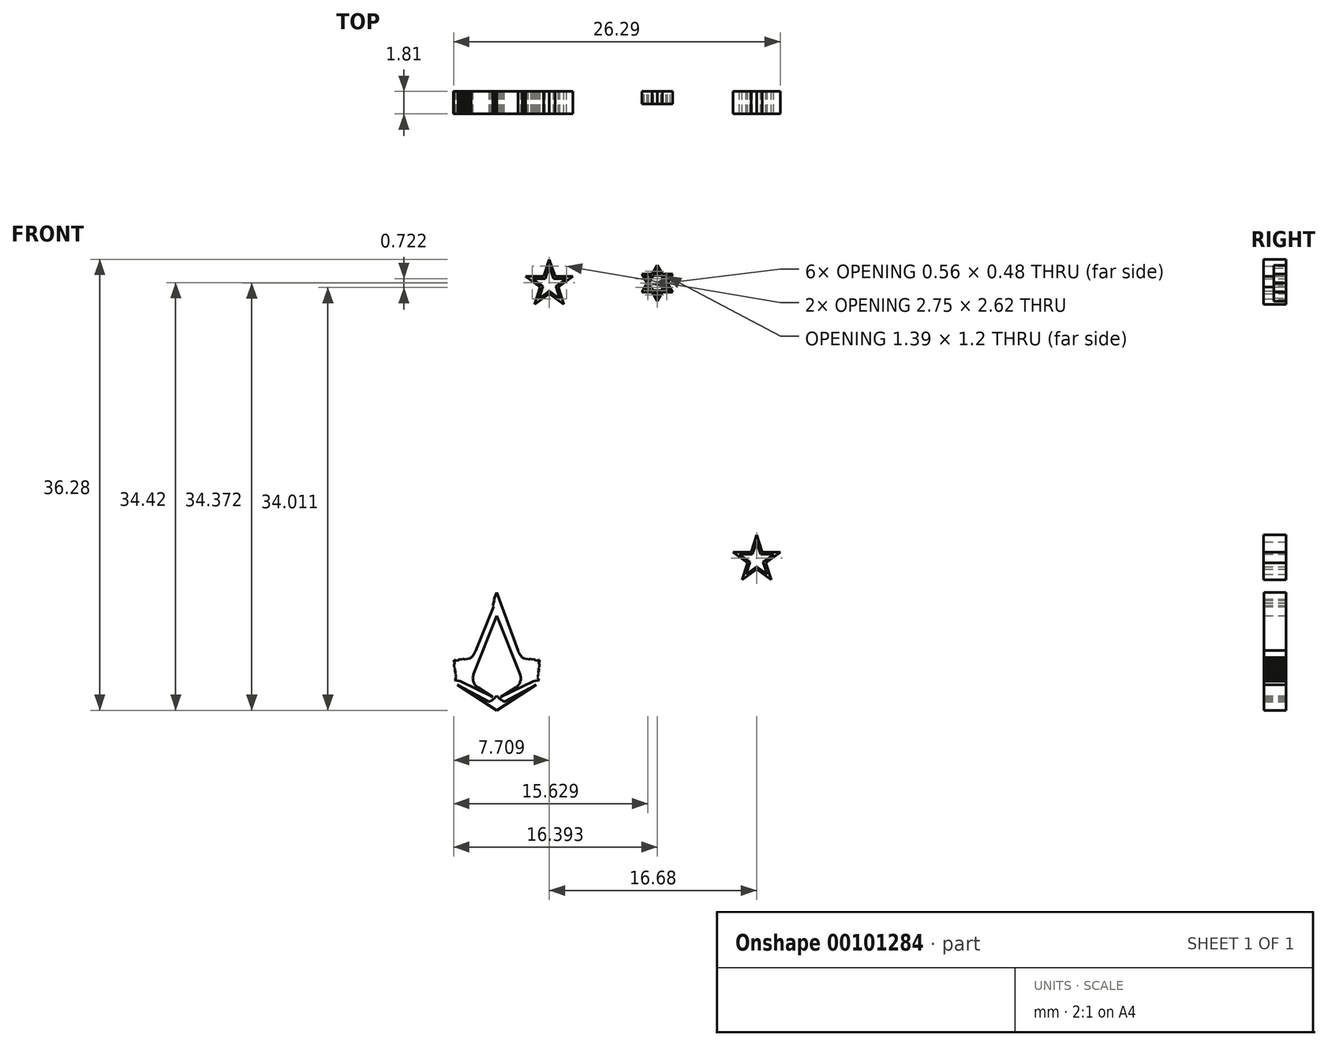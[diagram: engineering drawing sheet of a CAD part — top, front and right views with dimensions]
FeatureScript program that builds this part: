
annotation { "Feature Type Name" : "Feature", "Feature Type Description" : "" }
export const myFeature = defineFeature(function(context is Context, id is Id, definition is map)
    precondition{}
    {
        {
            var Q0;
            Q0=qCreatedBy(makeId("Front.planeOp"),FACE);
            var sketch = newSketch(context, id + "F0", { "sketchPlane" : qUnion([Q0])});
            skLineSegment(sketch, "E0", {"start": v(-3.78, 9.8) * mm, "end": v(-3.78, -0.73) * mm});
            skLineSegment(sketch, "E1", {"start": v(-3.78, 9.8) * mm, "end": v(-3.78, 11.8) * mm});
            skLineSegment(sketch, "E2", {"start": v(-3.78, 9.8) * mm, "end": v(-4, 9.25) * mm});
            skLineSegment(sketch, "E3", {"start": v(-4, 9.25) * mm, "end": v(-3.96, 9.16) * mm});
            skLineSegment(sketch, "E4", {"start": v(-3.96, 9.16) * mm, "end": v(-4.04, 8.97) * mm});
            skLineSegment(sketch, "E5", {"start": v(-4.04, 8.97) * mm, "end": v(-4.02, 8.93) * mm});
            skLineSegment(sketch, "E6", {"start": v(-4.02, 8.93) * mm, "end": v(-4.1, 8.75) * mm});
            skLineSegment(sketch, "E7", {"start": v(-4.1, 8.75) * mm, "end": v(-4.05, 8.65) * mm});
            skLineSegment(sketch, "E8", {"start": v(-4.05, 8.65) * mm, "end": v(-5.48, 5.12) * mm});
            skArc(sketch, "E9", {"start": v(-5.84, 4.56) * mm, "mid": v(-5.63, 4.83) * mm, "end": v(-5.48, 5.12) * mm});
            skArc(sketch, "E10", {"start": v(-6.03, 4.5) * mm, "mid": v(-5.92, 4.51) * mm, "end": v(-5.84, 4.56) * mm});
            skLineSegment(sketch, "E11", {"start": v(-6.03, 4.5) * mm, "end": v(-6.09, 4.43) * mm});
            skLineSegment(sketch, "E12", {"start": v(-6.09, 4.43) * mm, "end": v(-6.24, 4.47) * mm});
            skLineSegment(sketch, "E13", {"start": v(-6.24, 4.47) * mm, "end": v(-6.32, 4.39) * mm});
            skLineSegment(sketch, "E14", {"start": v(-6.32, 4.39) * mm, "end": v(-6.53, 4.46) * mm});
            skLineSegment(sketch, "E15", {"start": v(-6.53, 4.46) * mm, "end": v(-6.6, 4.4) * mm});
            skLineSegment(sketch, "E16", {"start": v(-6.6, 4.4) * mm, "end": v(-6.79, 4.45) * mm});
            skLineSegment(sketch, "E17", {"start": v(-6.79, 4.45) * mm, "end": v(-6.9, 4.3) * mm});
            skLineSegment(sketch, "E18", {"start": v(-6.9, 4.3) * mm, "end": v(-7.24, 4.37) * mm});
            skLineSegment(sketch, "E19", {"start": v(-7.24, 4.37) * mm, "end": v(-7.18, 4.16) * mm});
            skLineSegment(sketch, "E20", {"start": v(-7.18, 4.16) * mm, "end": v(-7.18, 4.03) * mm});
            skLineSegment(sketch, "E21", {"start": v(-7.18, 4.03) * mm, "end": v(-7.26, 3.94) * mm});
            skLineSegment(sketch, "E22", {"start": v(-7.26, 3.94) * mm, "end": v(-7.14, 3.79) * mm});
            skLineSegment(sketch, "E23", {"start": v(-7.14, 3.79) * mm, "end": v(-7.21, 3.7) * mm});
            skLineSegment(sketch, "E24", {"start": v(-7.21, 3.7) * mm, "end": v(-7.1, 3.54) * mm});
            skLineSegment(sketch, "E25", {"start": v(-7.1, 3.54) * mm, "end": v(-7.18, 3.4) * mm});
            skLineSegment(sketch, "E26", {"start": v(-7.18, 3.4) * mm, "end": v(-7.07, 3.3) * mm});
            skLineSegment(sketch, "E27", {"start": v(-7.07, 3.3) * mm, "end": v(-7.13, 3.18) * mm});
            skLineSegment(sketch, "E28", {"start": v(-7.13, 3.18) * mm, "end": v(-7.07, 3.09) * mm});
            skLineSegment(sketch, "E29", {"start": v(-7.07, 3.09) * mm, "end": v(-7.1, 3.03) * mm});
            skLineSegment(sketch, "E30", {"start": v(-7.1, 3.03) * mm, "end": v(-7.06, 2.96) * mm});
            skLineSegment(sketch, "E31", {"start": v(-7.06, 2.96) * mm, "end": v(-7.1, 2.91) * mm});
            skLineSegment(sketch, "E32", {"start": v(-7.1, 2.91) * mm, "end": v(-7.08, 2.85) * mm});
            skLineSegment(sketch, "E33", {"start": v(-7.08, 2.85) * mm, "end": v(-7.19, 2.77) * mm});
            skLineSegment(sketch, "E34", {"start": v(-7.19, 2.77) * mm, "end": v(-6.72, 2.67) * mm});
            skLineSegment(sketch, "E35", {"start": v(-6.72, 2.67) * mm, "end": v(-4.1, 1.4) * mm});
            skLineSegment(sketch, "E36", {"start": v(-4.1, 1.4) * mm, "end": v(-5.28, 2.14) * mm});
            skArc(sketch, "E37", {"start": v(-5.71, 2.6) * mm, "mid": v(-5.53, 2.34) * mm, "end": v(-5.28, 2.14) * mm});
            skArc(sketch, "E38", {"start": v(-5.67, 3.16) * mm, "mid": v(-5.74, 2.88) * mm, "end": v(-5.71, 2.6) * mm});
            skLineSegment(sketch, "E39", {"start": v(-5.67, 3.16) * mm, "end": v(-3.78, 7.95) * mm});
            skLineSegment(sketch, "E40", {"start": v(-6.96, 2.37) * mm, "end": v(-4.4, 1) * mm});
            skLineSegment(sketch, "E41", {"start": v(-4.4, 1) * mm, "end": v(-4.37, 1.05) * mm});
            skLineSegment(sketch, "E42", {"start": v(-4.37, 1.05) * mm, "end": v(-4.3, 1.05) * mm});
            skLineSegment(sketch, "E43", {"start": v(-4.3, 1.05) * mm, "end": v(-4.27, 1.1) * mm});
            skLineSegment(sketch, "E44", {"start": v(-4.27, 1.1) * mm, "end": v(-4.18, 1.1) * mm});
            skLineSegment(sketch, "E45", {"start": v(-4.18, 1.1) * mm, "end": v(-4.15, 1.16) * mm});
            skLineSegment(sketch, "E46", {"start": v(-4.15, 1.16) * mm, "end": v(-4.1, 1.16) * mm});
            skLineSegment(sketch, "E47", {"start": v(-4.1, 1.16) * mm, "end": v(-4.08, 1.2) * mm});
            skLineSegment(sketch, "E48", {"start": v(-4.08, 1.2) * mm, "end": v(-4.03, 1.2) * mm});
            skLineSegment(sketch, "E49", {"start": v(-4.03, 1.2) * mm, "end": v(-4.01, 1.28) * mm});
            skLineSegment(sketch, "E50", {"start": v(-4.01, 1.28) * mm, "end": v(-3.96, 1.28) * mm});
            skLineSegment(sketch, "E51", {"start": v(-3.96, 1.28) * mm, "end": v(-3.92, 1.39) * mm});
            skLineSegment(sketch, "E52", {"start": v(-3.92, 1.39) * mm, "end": v(-3.84, 1.39) * mm});
            skLineSegment(sketch, "E53", {"start": v(-3.84, 1.39) * mm, "end": v(-3.78, 1.49) * mm});
            skLineSegment(sketch, "E54", {"start": v(-6.96, 2.37) * mm, "end": v(-3.78, 0.32) * mm});
            skLineSegment(sketch, "E55.MirrorCS", {"start": v(-3.29, 1.1) * mm, "end": v(-3.38, 1.1) * mm});
            skLineSegment(sketch, "E56.MirrorCS", {"start": v(-3.48, 1.2) * mm, "end": v(-3.53, 1.2) * mm});
            skLineSegment(sketch, "E57.MirrorCS", {"start": v(-3.38, 1.1) * mm, "end": v(-3.4, 1.16) * mm});
            skLineSegment(sketch, "E58.MirrorCS", {"start": v(-3.4, 1.16) * mm, "end": v(-3.46, 1.16) * mm});
            skLineSegment(sketch, "E59.MirrorCS", {"start": v(-3.46, 1.16) * mm, "end": v(-3.48, 1.2) * mm});
            skLineSegment(sketch, "E60.MirrorCS", {"start": v(-3.27, 1.05) * mm, "end": v(-3.29, 1.1) * mm});
            skLineSegment(sketch, "E61.MirrorCS", {"start": v(-3.55, 1.28) * mm, "end": v(-3.6, 1.28) * mm});
            skLineSegment(sketch, "E62.MirrorCS", {"start": v(-3.6, 1.28) * mm, "end": v(-3.64, 1.39) * mm});
            skLineSegment(sketch, "E63.MirrorCS", {"start": v(-3.18, 1.05) * mm, "end": v(-3.27, 1.05) * mm});
            skLineSegment(sketch, "E64.MirrorCS", {"start": v(-3.53, 1.2) * mm, "end": v(-3.55, 1.28) * mm});
            skLineSegment(sketch, "E65.MirrorCS", {"start": v(-0.5, 2.96) * mm, "end": v(-0.46, 2.91) * mm});
            skLineSegment(sketch, "E66.MirrorCS", {"start": v(-0.46, 3.03) * mm, "end": v(-0.5, 2.96) * mm});
            skLineSegment(sketch, "E67.MirrorCS", {"start": v(-0.46, 2.91) * mm, "end": v(-0.48, 2.85) * mm});
            skLineSegment(sketch, "E68.MirrorCS", {"start": v(-0.48, 2.85) * mm, "end": v(-0.37, 2.77) * mm});
            skLineSegment(sketch, "E69.MirrorCS", {"start": v(-0.5, 3.09) * mm, "end": v(-0.46, 3.03) * mm});
            skLineSegment(sketch, "E70.MirrorCS", {"start": v(-1.24, 4.39) * mm, "end": v(-1.03, 4.46) * mm});
            skLineSegment(sketch, "E71.MirrorCS", {"start": v(-0.43, 3.18) * mm, "end": v(-0.5, 3.09) * mm});
            skLineSegment(sketch, "E72.MirrorCS", {"start": v(-3.17, 1) * mm, "end": v(-3.18, 1.05) * mm});
            skLineSegment(sketch, "E73.MirrorCS", {"start": v(-1.47, 4.43) * mm, "end": v(-1.32, 4.47) * mm});
            skLineSegment(sketch, "E74.MirrorCS", {"start": v(-1.32, 4.47) * mm, "end": v(-1.24, 4.39) * mm});
            skLineSegment(sketch, "E75.MirrorCS", {"start": v(-3.64, 1.39) * mm, "end": v(-3.72, 1.39) * mm});
            skLineSegment(sketch, "E76.MirrorCS", {"start": v(-1.03, 4.46) * mm, "end": v(-0.96, 4.4) * mm});
            skLineSegment(sketch, "E77.MirrorCS", {"start": v(-0.5, 3.3) * mm, "end": v(-0.43, 3.18) * mm});
            skLineSegment(sketch, "E78.MirrorCS", {"start": v(-3.72, 1.39) * mm, "end": v(-3.78, 1.49) * mm});
            skLineSegment(sketch, "E79.MirrorCS", {"start": v(-0.38, 3.4) * mm, "end": v(-0.5, 3.3) * mm});
            skLineSegment(sketch, "E80.MirrorCS", {"start": v(-0.47, 3.54) * mm, "end": v(-0.38, 3.4) * mm});
            skLineSegment(sketch, "E81.MirrorCS", {"start": v(-0.34, 3.7) * mm, "end": v(-0.47, 3.54) * mm});
            skLineSegment(sketch, "E82.MirrorCS", {"start": v(-0.3, 3.94) * mm, "end": v(-0.42, 3.79) * mm});
            skLineSegment(sketch, "E83.MirrorCS", {"start": v(-0.37, 2.77) * mm, "end": v(-0.84, 2.67) * mm});
            skArc(sketch, "E84.MirrorCS", {"start": v(-1.72, 4.56) * mm, "mid": v(-1.93, 4.83) * mm, "end": v(-2.08, 5.12) * mm});
            skLineSegment(sketch, "E85.MirrorCS", {"start": v(-0.65, 4.3) * mm, "end": v(-0.32, 4.37) * mm});
            skArc(sketch, "E86.MirrorCS", {"start": v(-1.53, 4.5) * mm, "mid": v(-1.63, 4.51) * mm, "end": v(-1.72, 4.56) * mm});
            skLineSegment(sketch, "E87.MirrorCS", {"start": v(-1.53, 4.5) * mm, "end": v(-1.47, 4.43) * mm});
            skLineSegment(sketch, "E88.MirrorCS", {"start": v(-0.38, 4.03) * mm, "end": v(-0.3, 3.94) * mm});
            skLineSegment(sketch, "E89.MirrorCS", {"start": v(-0.96, 4.4) * mm, "end": v(-0.77, 4.45) * mm});
            skLineSegment(sketch, "E90.MirrorCS", {"start": v(-0.32, 4.37) * mm, "end": v(-0.38, 4.16) * mm});
            skLineSegment(sketch, "E91.MirrorCS", {"start": v(-0.42, 3.79) * mm, "end": v(-0.34, 3.7) * mm});
            skLineSegment(sketch, "E92.MirrorCS", {"start": v(-0.77, 4.45) * mm, "end": v(-0.65, 4.3) * mm});
            skLineSegment(sketch, "E93.MirrorCS", {"start": v(-0.38, 4.16) * mm, "end": v(-0.38, 4.03) * mm});
            skArc(sketch, "E94.MirrorCS", {"start": v(-1.9, 3.16) * mm, "mid": v(-1.82, 2.88) * mm, "end": v(-1.84, 2.6) * mm});
            skArc(sketch, "E95.MirrorCS", {"start": v(-1.84, 2.6) * mm, "mid": v(-2.03, 2.34) * mm, "end": v(-2.28, 2.14) * mm});
            skLineSegment(sketch, "E96.MirrorCS", {"start": v(-0.6, 2.37) * mm, "end": v(-3.78, 0.32) * mm});
            skLineSegment(sketch, "E97.MirrorCS", {"start": v(-0.84, 2.67) * mm, "end": v(-3.46, 1.4) * mm});
            skLineSegment(sketch, "E98.MirrorCS", {"start": v(-1.9, 3.16) * mm, "end": v(-3.78, 7.95) * mm});
            skLineSegment(sketch, "E99.MirrorCS", {"start": v(-0.6, 2.37) * mm, "end": v(-3.17, 1) * mm});
            skLineSegment(sketch, "E100.MirrorCS", {"start": v(-3.46, 1.4) * mm, "end": v(-2.28, 2.14) * mm});
            skLineSegment(sketch, "E101", {"start": v(-3.78, 9.8) * mm, "end": v(-2.08, 5.12) * mm});
            skSolve(sketch);
        }
        {
            var Q0;
            {var subQ0=sQuery(id+"F0.wireOp",EDGE,"E2");Q0=makeQuery(id+"F0.imprint","IMPRINT",FACE,{"disambiguationData":[TD([[makeQuery(id+"F0.imprint","IMPRINT",EDGE,{"derivedFrom":subQ0}),1.0]])]});}
            var Q1;
            Q1=makeQuery(id+"F0.imprint","IMPRINT",FACE,{"disambiguationData":[TD([[makeQuery(id+"F0.imprint","IMPRINT",EDGE,{"derivedFrom":sQuery(id+"F0.wireOp",EDGE,"E65.MirrorCS")}),-1.0]])]});
            var Q2;
            Q2=makeQuery(id+"F0.imprint","IMPRINT",FACE,{"disambiguationData":[TD([[makeQuery(id+"F0.imprint","IMPRINT",EDGE,{"derivedFrom":sQuery(id+"F0.wireOp",EDGE,"E40")}),-1.0]])]});
            var Q3;
            Q3=makeQuery(id+"F0.imprint","IMPRINT",FACE,{"disambiguationData":[TD([[makeQuery(id+"F0.imprint","IMPRINT",EDGE,{"derivedFrom":sQuery(id+"F0.wireOp",EDGE,"E55.MirrorCS")}),1.0]])]});
            extrude(context, id + "F1", {"entities" : qUnion([Q0, Q1, Q2, Q3]), "depth" : 1.8 * mm});
        }
        {
            var Q0;
            Q0=qCreatedBy(makeId("Front.planeOp"),FACE);
            var sketch = newSketch(context, id + "F2", { "sketchPlane" : qUnion([Q0])});
            skLineSegment(sketch, "E102", {"start": v(-0.28, 34.37) * mm, "end": v(-1.45, 35.22) * mm});
            skLineSegment(sketch, "E103", {"start": v(0, 35.22) * mm, "end": v(-1.45, 35.22) * mm});
            skLineSegment(sketch, "E104", {"start": v(0, 35.22) * mm, "end": v(0.45, 36.6) * mm});
            skLineSegment(sketch, "E105", {"start": v(-0.28, 34.37) * mm, "end": v(-0.73, 32.98) * mm});
            skLineSegment(sketch, "E106", {"start": v(-0.73, 32.98) * mm, "end": v(0.45, 33.84) * mm});
            skLineSegment(sketch, "E107.MirrorCS", {"start": v(0.9, 35.22) * mm, "end": v(0.45, 36.6) * mm});
            skLineSegment(sketch, "E108.MirrorCS", {"start": v(0.9, 35.22) * mm, "end": v(2.35, 35.22) * mm});
            skLineSegment(sketch, "E109.MirrorCS", {"start": v(1.18, 34.37) * mm, "end": v(2.35, 35.22) * mm});
            skLineSegment(sketch, "E110.MirrorCS", {"start": v(1.62, 32.98) * mm, "end": v(0.45, 33.84) * mm});
            skLineSegment(sketch, "E111.MirrorCS", {"start": v(1.18, 34.37) * mm, "end": v(1.62, 32.98) * mm});
            skLineSegment(sketch, "E112", {"start": v(0.45, 36.6) * mm, "end": v(0.45, 33.84) * mm});
            skLineSegment(sketch, "E113", {"start": v(0.45, 36.6) * mm, "end": v(0.45, 36.05) * mm});
            skCircle(sketch, "E114", {"center": v(0.45, 34.6) * mm, "radius": 2 * mm});
            skLineSegment(sketch, "E115", {"start": v(1.62, 32.98) * mm, "end": v(0, 35.22) * mm});
            skLineSegment(sketch, "E116", {"start": v(0.45, 36.05) * mm, "end": v(0.12, 35.05) * mm});
            skLineSegment(sketch, "E117", {"start": v(-1.45, 35.22) * mm, "end": v(1.18, 34.37) * mm});
            skLineSegment(sketch, "E118", {"start": v(2.35, 35.22) * mm, "end": v(-0.28, 34.37) * mm});
            skLineSegment(sketch, "E119", {"start": v(-0.73, 32.98) * mm, "end": v(0.9, 35.22) * mm});
            skLineSegment(sketch, "E120", {"start": v(0.12, 35.05) * mm, "end": v(-0.93, 35.05) * mm});
            skLineSegment(sketch, "E121", {"start": v(-0.93, 35.05) * mm, "end": v(-0.08, 34.43) * mm});
            skLineSegment(sketch, "E122.MirrorCS", {"start": v(-0.4, 33.43) * mm, "end": v(-0.08, 34.43) * mm});
            skLineSegment(sketch, "E123", {"start": v(-0.4, 33.43) * mm, "end": v(0.45, 34.05) * mm});
            skLineSegment(sketch, "E124.MirrorCS", {"start": v(0.45, 36.05) * mm, "end": v(0.77, 35.05) * mm});
            skLineSegment(sketch, "E125.MirrorCS", {"start": v(0.77, 35.05) * mm, "end": v(1.83, 35.05) * mm});
            skLineSegment(sketch, "E126.MirrorCS", {"start": v(1.83, 35.05) * mm, "end": v(0.97, 34.43) * mm});
            skLineSegment(sketch, "E127.MirrorCS", {"start": v(1.3, 33.43) * mm, "end": v(0.97, 34.43) * mm});
            skLineSegment(sketch, "E128.MirrorCS", {"start": v(1.3, 33.43) * mm, "end": v(0.45, 34.05) * mm});
            skSolve(sketch);
        }
        {
            var Q0;
            {var subQ0=sQuery(id+"F2.wireOp",EDGE,"E127.MirrorCS");Q0=makeQuery(id+"F2.imprint","IMPRINT",FACE,{"disambiguationData":[TD([[makeQuery(id+"F2.imprint","IMPRINT",EDGE,{"derivedFrom":subQ0}),1.0]])]});}
            var Q1;
            {var subQ0=sQuery(id+"F2.wireOp",EDGE,"E126.MirrorCS");Q1=makeQuery(id+"F2.imprint","IMPRINT",FACE,{"disambiguationData":[TD([[makeQuery(id+"F2.imprint","IMPRINT",EDGE,{"derivedFrom":subQ0}),-1.0]])]});}
            var Q2;
            {var subQ0=sQuery(id+"F2.wireOp",EDGE,"E123");Q2=makeQuery(id+"F2.imprint","IMPRINT",FACE,{"disambiguationData":[TD([[makeQuery(id+"F2.imprint","IMPRINT",EDGE,{"derivedFrom":subQ0}),1.0]])]});}
            var Q3;
            {var subQ0=sQuery(id+"F2.wireOp",EDGE,"E128.MirrorCS");Q3=makeQuery(id+"F2.imprint","IMPRINT",FACE,{"disambiguationData":[TD([[makeQuery(id+"F2.imprint","IMPRINT",EDGE,{"derivedFrom":subQ0}),-1.0]])]});}
            var Q4;
            {var subQ0=sQuery(id+"F2.wireOp",EDGE,"E125.MirrorCS");Q4=makeQuery(id+"F2.imprint","IMPRINT",FACE,{"disambiguationData":[TD([[makeQuery(id+"F2.imprint","IMPRINT",EDGE,{"derivedFrom":subQ0}),-1.0]])]});}
            var Q5;
            {var subQ0=sQuery(id+"F2.wireOp",EDGE,"E122.MirrorCS");Q5=makeQuery(id+"F2.imprint","IMPRINT",FACE,{"disambiguationData":[TD([[makeQuery(id+"F2.imprint","IMPRINT",EDGE,{"derivedFrom":subQ0}),-1.0]])]});}
            var Q6;
            {var subQ0=sQuery(id+"F2.wireOp",EDGE,"E124.MirrorCS");Q6=makeQuery(id+"F2.imprint","IMPRINT",FACE,{"disambiguationData":[TD([[makeQuery(id+"F2.imprint","IMPRINT",EDGE,{"derivedFrom":subQ0}),-1.0]])]});}
            var Q7;
            {var subQ0=sQuery(id+"F2.wireOp",EDGE,"E116");Q7=makeQuery(id+"F2.imprint","IMPRINT",FACE,{"disambiguationData":[TD([[makeQuery(id+"F2.imprint","IMPRINT",EDGE,{"derivedFrom":subQ0}),1.0]])]});}
            var Q8;
            {var subQ0=sQuery(id+"F2.wireOp",EDGE,"E120");Q8=makeQuery(id+"F2.imprint","IMPRINT",FACE,{"disambiguationData":[TD([[makeQuery(id+"F2.imprint","IMPRINT",EDGE,{"derivedFrom":subQ0}),1.0]])]});}
            var Q9;
            {var subQ0=sQuery(id+"F2.wireOp",EDGE,"E121");Q9=makeQuery(id+"F2.imprint","IMPRINT",FACE,{"disambiguationData":[TD([[makeQuery(id+"F2.imprint","IMPRINT",EDGE,{"derivedFrom":subQ0}),1.0]])]});}
            extrude(context, id + "F3", {"entities" : qUnion([Q0, Q1, Q2, Q3, Q4, Q5, Q6, Q7, Q8, Q9]), "depth" : 1.8 * mm});
        }
        {
            var Q0;
            {var subQ0=sQuery(id+"F2.wireOp",EDGE,"E104");Q0=makeQuery(id+"F2.imprint","IMPRINT",FACE,{"disambiguationData":[TD([[makeQuery(id+"F2.imprint","IMPRINT",EDGE,{"derivedFrom":subQ0}),-1.0]])]});}
            var Q1;
            {var subQ0=sQuery(id+"F2.wireOp",EDGE,"E107.MirrorCS");Q1=makeQuery(id+"F2.imprint","IMPRINT",FACE,{"disambiguationData":[TD([[makeQuery(id+"F2.imprint","IMPRINT",EDGE,{"derivedFrom":subQ0}),1.0]])]});}
            var Q2;
            {var subQ0=sQuery(id+"F2.wireOp",EDGE,"E108.MirrorCS");Q2=makeQuery(id+"F2.imprint","IMPRINT",FACE,{"disambiguationData":[TD([[makeQuery(id+"F2.imprint","IMPRINT",EDGE,{"derivedFrom":subQ0}),-1.0]])]});}
            var Q3;
            {var subQ0=sQuery(id+"F2.wireOp",EDGE,"E109.MirrorCS");Q3=makeQuery(id+"F2.imprint","IMPRINT",FACE,{"disambiguationData":[TD([[makeQuery(id+"F2.imprint","IMPRINT",EDGE,{"derivedFrom":subQ0}),1.0]])]});}
            var Q4;
            {var subQ0=sQuery(id+"F2.wireOp",EDGE,"E111.MirrorCS");Q4=makeQuery(id+"F2.imprint","IMPRINT",FACE,{"disambiguationData":[TD([[makeQuery(id+"F2.imprint","IMPRINT",EDGE,{"derivedFrom":subQ0}),-1.0]])]});}
            var Q5;
            {var subQ0=sQuery(id+"F2.wireOp",EDGE,"E110.MirrorCS");Q5=makeQuery(id+"F2.imprint","IMPRINT",FACE,{"disambiguationData":[TD([[makeQuery(id+"F2.imprint","IMPRINT",EDGE,{"derivedFrom":subQ0}),-1.0]])]});}
            var Q6;
            {var subQ0=sQuery(id+"F2.wireOp",EDGE,"E106");Q6=makeQuery(id+"F2.imprint","IMPRINT",FACE,{"disambiguationData":[TD([[makeQuery(id+"F2.imprint","IMPRINT",EDGE,{"derivedFrom":subQ0}),1.0]])]});}
            var Q7;
            {var subQ0=sQuery(id+"F2.wireOp",EDGE,"E105");Q7=makeQuery(id+"F2.imprint","IMPRINT",FACE,{"disambiguationData":[TD([[makeQuery(id+"F2.imprint","IMPRINT",EDGE,{"derivedFrom":subQ0}),1.0]])]});}
            var Q8;
            {var subQ0=sQuery(id+"F2.wireOp",EDGE,"E102");Q8=makeQuery(id+"F2.imprint","IMPRINT",FACE,{"disambiguationData":[TD([[makeQuery(id+"F2.imprint","IMPRINT",EDGE,{"derivedFrom":subQ0}),-1.0]])]});}
            var Q9;
            {var subQ0=sQuery(id+"F2.wireOp",EDGE,"E103");Q9=makeQuery(id+"F2.imprint","IMPRINT",FACE,{"disambiguationData":[TD([[makeQuery(id+"F2.imprint","IMPRINT",EDGE,{"derivedFrom":subQ0}),1.0]])]});}
            extrude(context, id + "F4", {"entities" : qUnion([Q0, Q1, Q2, Q3, Q4, Q5, Q6, Q7, Q8, Q9]), "depth" : 1.81 * mm});
        }
        {
            var Q0;
            Q0=makeQuery(id+"F1.opExtrude","SWEPT_EDGE",EDGE,{"disambiguationData":[OSD([sQuery(id+"F0.wireOp",EDGE,"E37"),sQuery(id+"F0.wireOp",EDGE,"E38")])]});
            var Q1;
            Q1=makeQuery(id+"F1.opExtrude","SWEPT_EDGE",EDGE,{"disambiguationData":[OSD([sQuery(id+"F0.wireOp",EDGE,"E94.MirrorCS"),sQuery(id+"F0.wireOp",EDGE,"E95.MirrorCS")])]});
            fillet(context, id + "F5", {"entities" : qUnion([Q0, Q1]), "radius" : 0.9 * mm, "tangentPropagation" : true, "allowEdgeOverflow" : false});
        }
        {
            var Q0;
            Q0=qCreatedBy(makeId("Front.planeOp"),FACE);
            var sketch = newSketch(context, id + "F6", { "sketchPlane" : qUnion([Q0])});
            skLineSegment(sketch, "E129", {"start": v(9.13, 36.14) * mm, "end": v(7.88, 33.97) * mm});
            skLineSegment(sketch, "E130", {"start": v(7.88, 33.97) * mm, "end": v(10.38, 33.97) * mm});
            skLineSegment(sketch, "E131", {"start": v(9.13, 36.14) * mm, "end": v(10.38, 33.97) * mm});
            skLineSegment(sketch, "E132.top", {"start": v(7.88, 35.41) * mm, "end": v(10.38, 35.41) * mm});
            skLineSegment(sketch, "E133", {"start": v(7.88, 35.41) * mm, "end": v(9.13, 33.25) * mm});
            skLineSegment(sketch, "E134", {"start": v(10.38, 35.41) * mm, "end": v(9.13, 33.25) * mm});
            skLineSegment(sketch, "E135", {"start": v(9.13, 36.14) * mm, "end": v(9.13, 33.25) * mm});
            skPoint(sketch, "E136", {"position": v(9.97, 34.7) * mm});
            skLineSegment(sketch, "E137", {"start": v(8.3, 34.7) * mm, "end": v(9.97, 34.7) * mm});
            skLineSegment(sketch, "E138", {"start": v(7.88, 35.41) * mm, "end": v(8.1, 35.3) * mm});
            skLineSegment(sketch, "E139", {"start": v(8.72, 35.41) * mm, "end": v(8.5, 35.3) * mm});
            skLineSegment(sketch, "E140", {"start": v(8.3, 34.7) * mm, "end": v(8.3, 34.93) * mm});
            skLineSegment(sketch, "E141", {"start": v(8.1, 35.3) * mm, "end": v(8.5, 35.3) * mm});
            skLineSegment(sketch, "E142", {"start": v(8.3, 34.93) * mm, "end": v(8.5, 35.3) * mm});
            skLineSegment(sketch, "E143", {"start": v(8.1, 35.3) * mm, "end": v(8.3, 34.93) * mm});
            skLineSegment(sketch, "E144.MirrorCS", {"start": v(8.3, 34.45) * mm, "end": v(8.5, 34.1) * mm});
            skLineSegment(sketch, "E145.MirrorCS", {"start": v(8.1, 34.1) * mm, "end": v(8.3, 34.45) * mm});
            skLineSegment(sketch, "E146.MirrorCS", {"start": v(8.1, 34.1) * mm, "end": v(8.5, 34.1) * mm});
            skLineSegment(sketch, "E147.MirrorCS", {"start": v(9.97, 34.93) * mm, "end": v(9.76, 35.3) * mm});
            skLineSegment(sketch, "E148.MirrorCS", {"start": v(10.17, 35.3) * mm, "end": v(9.76, 35.3) * mm});
            skLineSegment(sketch, "E149.MirrorCS", {"start": v(10.17, 35.3) * mm, "end": v(9.97, 34.93) * mm});
            skLineSegment(sketch, "E150.MirrorCS", {"start": v(9.97, 34.45) * mm, "end": v(9.76, 34.1) * mm});
            skLineSegment(sketch, "E151.MirrorCS", {"start": v(10.17, 34.1) * mm, "end": v(9.97, 34.45) * mm});
            skLineSegment(sketch, "E152.MirrorCS", {"start": v(10.17, 34.1) * mm, "end": v(9.76, 34.1) * mm});
            skLineSegment(sketch, "E153.MirrorCS", {"start": v(9.13, 35.9) * mm, "end": v(8.92, 35.53) * mm});
            skLineSegment(sketch, "E154.MirrorCS", {"start": v(9.13, 35.9) * mm, "end": v(9.34, 35.53) * mm});
            skLineSegment(sketch, "E155.MirrorCS", {"start": v(9.34, 35.53) * mm, "end": v(8.92, 35.53) * mm});
            skLineSegment(sketch, "E156.MirrorCS", {"start": v(9.34, 33.85) * mm, "end": v(8.92, 33.85) * mm});
            skLineSegment(sketch, "E157.MirrorCS", {"start": v(9.13, 33.49) * mm, "end": v(9.34, 33.85) * mm});
            skLineSegment(sketch, "E158.MirrorCS", {"start": v(9.13, 33.49) * mm, "end": v(8.92, 33.85) * mm});
            skLineSegment(sketch, "E159", {"start": v(8.92, 35.53) * mm, "end": v(8.3, 34.45) * mm});
            skLineSegment(sketch, "E160", {"start": v(8.5, 34.1) * mm, "end": v(9.76, 34.1) * mm});
            skLineSegment(sketch, "E161", {"start": v(8.3, 34.93) * mm, "end": v(8.92, 33.85) * mm});
            skLineSegment(sketch, "E162", {"start": v(9.34, 33.85) * mm, "end": v(9.97, 34.93) * mm});
            skLineSegment(sketch, "E163", {"start": v(8.5, 35.3) * mm, "end": v(9.76, 35.3) * mm});
            skLineSegment(sketch, "E164", {"start": v(9.97, 34.45) * mm, "end": v(9.34, 35.53) * mm});
            skLineSegment(sketch, "E165", {"start": v(8.4, 35.11) * mm, "end": v(8.61, 35) * mm});
            skLineSegment(sketch, "E166", {"start": v(8.1, 35.05) * mm, "end": v(8.2, 35.1) * mm});
            skSolve(sketch);
        }
        {
            var Q0;
            {var subQ6=sQuery(id+"F6.wireOp",EDGE,"E145.MirrorCS");Q0=makeQuery(id+"F6.imprint","IMPRINT",FACE,{"disambiguationData":[TD([[makeQuery(id+"F6.imprint","IMPRINT",EDGE,{"derivedFrom":subQ6}),1.0]])]});}
            var Q1;
            {var subQ0=sQuery(id+"F6.wireOp",EDGE,"E138");Q1=makeQuery(id+"F6.imprint","IMPRINT",FACE,{"disambiguationData":[TD([[makeQuery(id+"F6.imprint","IMPRINT",EDGE,{"derivedFrom":subQ0}),-1.0]])]});}
            var Q2;
            {var subQ0=sQuery(id+"F6.wireOp",EDGE,"E138");Q2=makeQuery(id+"F6.imprint","IMPRINT",FACE,{"disambiguationData":[TD([[makeQuery(id+"F6.imprint","IMPRINT",EDGE,{"derivedFrom":subQ0}),1.0]])]});}
            var Q3;
            {var subQ0=sQuery(id+"F6.wireOp",EDGE,"E140");Q3=makeQuery(id+"F6.imprint","IMPRINT",FACE,{"disambiguationData":[TD([[makeQuery(id+"F6.imprint","IMPRINT",EDGE,{"derivedFrom":subQ0}),1.0]])]});}
            var Q4;
            {var subQ0=sQuery(id+"F6.wireOp",EDGE,"E140");Q4=makeQuery(id+"F6.imprint","IMPRINT",FACE,{"disambiguationData":[TD([[makeQuery(id+"F6.imprint","IMPRINT",EDGE,{"derivedFrom":subQ0}),-1.0]])]});}
            var Q5;
            {var subQ0=sQuery(id+"F6.wireOp",EDGE,"E139");Q5=makeQuery(id+"F6.imprint","IMPRINT",FACE,{"disambiguationData":[TD([[makeQuery(id+"F6.imprint","IMPRINT",EDGE,{"derivedFrom":subQ0}),1.0]])]});}
            var Q6;
            {var subQ0=sQuery(id+"F6.wireOp",EDGE,"E165");var subQ1=sQuery(id+"F6.wireOp",EDGE,"E129");var subQ2=makeQuery(id+"F6.imprint","INTERSECT",VERTEX,{"derivedFrom":[subQ1,subQ0]});Q6=makeQuery(id+"F6.imprint","IMPRINT",FACE,{"disambiguationData":[TD([[makeQuery(id+"F6.imprint","IMPRINT",EDGE,{"disambiguationData":[TD([[subQ2,-1.0]])],"derivedFrom":subQ1}),1.0]])]});}
            var Q7;
            {var subQ0=sQuery(id+"F6.wireOp",EDGE,"E163");var subQ1=sQuery(id+"F6.wireOp",EDGE,"E129");var subQ2=makeQuery(id+"F6.imprint","INTERSECT",VERTEX,{"derivedFrom":[subQ1,subQ0]});Q7=makeQuery(id+"F6.imprint","IMPRINT",FACE,{"disambiguationData":[TD([[makeQuery(id+"F6.imprint","IMPRINT",EDGE,{"disambiguationData":[TD([[subQ2,-1.0]])],"derivedFrom":subQ1}),1.0]])]});}
            var Q8;
            {var subQ0=sQuery(id+"F6.wireOp",EDGE,"E132.top");var subQ5=sQuery(id+"F6.wireOp",EDGE,"E159");var subQ6=makeQuery(id+"F6.imprint","INTERSECT",VERTEX,{"derivedFrom":[subQ0,subQ5]});Q8=makeQuery(id+"F6.imprint","IMPRINT",FACE,{"disambiguationData":[TD([[makeQuery(id+"F6.imprint","IMPRINT",EDGE,{"disambiguationData":[TD([[subQ6,-1.0]])],"derivedFrom":subQ5}),-1.0]])]});}
            var Q9;
            {var subQ0=sQuery(id+"F6.wireOp",EDGE,"E159");var subQ1=sQuery(id+"F6.wireOp",EDGE,"E133");var subQ2=makeQuery(id+"F6.imprint","INTERSECT",VERTEX,{"derivedFrom":[subQ1,subQ0]});Q9=makeQuery(id+"F6.imprint","IMPRINT",FACE,{"disambiguationData":[TD([[makeQuery(id+"F6.imprint","IMPRINT",EDGE,{"disambiguationData":[TD([[subQ2,-1.0]])],"derivedFrom":subQ1}),1.0]])]});}
            var Q10;
            {var subQ0=sQuery(id+"F6.wireOp",EDGE,"E133");var subQ1=sQuery(id+"F6.wireOp",EDGE,"E130");var subQ2=makeQuery(id+"F6.imprint","INTERSECT",VERTEX,{"derivedFrom":[subQ1,subQ0]});Q10=makeQuery(id+"F6.imprint","IMPRINT",FACE,{"disambiguationData":[TD([[makeQuery(id+"F6.imprint","IMPRINT",EDGE,{"disambiguationData":[TD([[subQ2,-1.0]])],"derivedFrom":subQ1}),1.0]])]});}
            var Q11;
            {var subQ1=sQuery(id+"F6.wireOp",EDGE,"E133");var subQ3=sQuery(id+"F6.wireOp",EDGE,"E159");var subQ4=makeQuery(id+"F6.imprint","INTERSECT",VERTEX,{"derivedFrom":[subQ1,subQ3]});Q11=makeQuery(id+"F6.imprint","IMPRINT",FACE,{"disambiguationData":[TD([[makeQuery(id+"F6.imprint","IMPRINT",EDGE,{"disambiguationData":[TD([[subQ4,1.0]])],"derivedFrom":subQ3}),-1.0]])]});}
            var Q12;
            {var subQ1=sQuery(id+"F6.wireOp",EDGE,"E129");var subQ3=sQuery(id+"F6.wireOp",EDGE,"E161");var subQ4=makeQuery(id+"F6.imprint","INTERSECT",VERTEX,{"derivedFrom":[subQ1,subQ3]});Q12=makeQuery(id+"F6.imprint","IMPRINT",FACE,{"disambiguationData":[TD([[makeQuery(id+"F6.imprint","IMPRINT",EDGE,{"disambiguationData":[TD([[subQ4,-1.0]])],"derivedFrom":subQ3}),-1.0]])]});}
            var Q13;
            {var subQ3=sQuery(id+"F6.wireOp",EDGE,"E158.MirrorCS");Q13=makeQuery(id+"F6.imprint","IMPRINT",FACE,{"disambiguationData":[TD([[makeQuery(id+"F6.imprint","IMPRINT",EDGE,{"derivedFrom":subQ3}),1.0]])]});}
            var Q14;
            {var subQ0=sQuery(id+"F6.wireOp",EDGE,"E161");var subQ1=sQuery(id+"F6.wireOp",EDGE,"E130");var subQ2=makeQuery(id+"F6.imprint","INTERSECT",VERTEX,{"derivedFrom":[subQ1,subQ0]});Q14=makeQuery(id+"F6.imprint","IMPRINT",FACE,{"disambiguationData":[TD([[makeQuery(id+"F6.imprint","IMPRINT",EDGE,{"disambiguationData":[TD([[subQ2,-1.0]])],"derivedFrom":subQ1}),1.0]])]});}
            var Q15;
            {var subQ0=sQuery(id+"F6.wireOp",EDGE,"E135");var subQ1=sQuery(id+"F6.wireOp",EDGE,"E130");var subQ2=makeQuery(id+"F6.imprint","INTERSECT",VERTEX,{"derivedFrom":[subQ1,subQ0]});Q15=makeQuery(id+"F6.imprint","IMPRINT",FACE,{"disambiguationData":[TD([[makeQuery(id+"F6.imprint","IMPRINT",EDGE,{"disambiguationData":[TD([[subQ2,-1.0]])],"derivedFrom":subQ1}),1.0]])]});}
            var Q16;
            {var subQ0=sQuery(id+"F6.wireOp",EDGE,"E157.MirrorCS");Q16=makeQuery(id+"F6.imprint","IMPRINT",FACE,{"disambiguationData":[TD([[makeQuery(id+"F6.imprint","IMPRINT",EDGE,{"derivedFrom":subQ0}),-1.0]])]});}
            var Q17;
            {var subQ0=sQuery(id+"F6.wireOp",EDGE,"E134");var subQ1=sQuery(id+"F6.wireOp",EDGE,"E130");var subQ2=makeQuery(id+"F6.imprint","INTERSECT",VERTEX,{"derivedFrom":[subQ1,subQ0]});Q17=makeQuery(id+"F6.imprint","IMPRINT",FACE,{"disambiguationData":[TD([[makeQuery(id+"F6.imprint","IMPRINT",EDGE,{"disambiguationData":[TD([[subQ2,1.0]])],"derivedFrom":subQ1}),1.0]])]});}
            var Q18;
            {var subQ8=sQuery(id+"F6.wireOp",EDGE,"E151.MirrorCS");Q18=makeQuery(id+"F6.imprint","IMPRINT",FACE,{"disambiguationData":[TD([[makeQuery(id+"F6.imprint","IMPRINT",EDGE,{"derivedFrom":subQ8}),-1.0]])]});}
            var Q19;
            {var subQ0=sQuery(id+"F6.wireOp",EDGE,"E164");var subQ1=sQuery(id+"F6.wireOp",EDGE,"E134");var subQ2=makeQuery(id+"F6.imprint","INTERSECT",VERTEX,{"derivedFrom":[subQ1,subQ0]});Q19=makeQuery(id+"F6.imprint","IMPRINT",FACE,{"disambiguationData":[TD([[makeQuery(id+"F6.imprint","IMPRINT",EDGE,{"disambiguationData":[TD([[subQ2,-1.0]])],"derivedFrom":subQ1}),-1.0]])]});}
            var Q20;
            {var subQ1=sQuery(id+"F6.wireOp",EDGE,"E134");var subQ3=sQuery(id+"F6.wireOp",EDGE,"E164");var subQ4=makeQuery(id+"F6.imprint","INTERSECT",VERTEX,{"derivedFrom":[subQ1,subQ3]});Q20=makeQuery(id+"F6.imprint","IMPRINT",FACE,{"disambiguationData":[TD([[makeQuery(id+"F6.imprint","IMPRINT",EDGE,{"disambiguationData":[TD([[subQ4,1.0]])],"derivedFrom":subQ1}),-1.0]])]});}
            var Q21;
            {var subQ1=sQuery(id+"F6.wireOp",EDGE,"E131");var subQ3=sQuery(id+"F6.wireOp",EDGE,"E162");var subQ4=makeQuery(id+"F6.imprint","INTERSECT",VERTEX,{"derivedFrom":[subQ1,subQ3]});Q21=makeQuery(id+"F6.imprint","IMPRINT",FACE,{"disambiguationData":[TD([[makeQuery(id+"F6.imprint","IMPRINT",EDGE,{"disambiguationData":[TD([[subQ4,-1.0]])],"derivedFrom":subQ1}),-1.0]])]});}
            var Q22;
            {var subQ0=sQuery(id+"F6.wireOp",EDGE,"E163");var subQ1=sQuery(id+"F6.wireOp",EDGE,"E131");var subQ2=makeQuery(id+"F6.imprint","INTERSECT",VERTEX,{"derivedFrom":[subQ1,subQ0]});Q22=makeQuery(id+"F6.imprint","IMPRINT",FACE,{"disambiguationData":[TD([[makeQuery(id+"F6.imprint","IMPRINT",EDGE,{"disambiguationData":[TD([[subQ2,-1.0]])],"derivedFrom":subQ1}),-1.0]])]});}
            var Q23;
            {var subQ12=sQuery(id+"F6.wireOp",EDGE,"E148.MirrorCS");Q23=makeQuery(id+"F6.imprint","IMPRINT",FACE,{"disambiguationData":[TD([[makeQuery(id+"F6.imprint","IMPRINT",EDGE,{"derivedFrom":subQ12}),-1.0]])]});}
            var Q24;
            {var subQ0=sQuery(id+"F6.wireOp",EDGE,"E132.top");var subQ1=sQuery(id+"F6.wireOp",EDGE,"E131");var subQ2=makeQuery(id+"F6.imprint","INTERSECT",VERTEX,{"derivedFrom":[subQ1,subQ0]});Q24=makeQuery(id+"F6.imprint","IMPRINT",FACE,{"disambiguationData":[TD([[makeQuery(id+"F6.imprint","IMPRINT",EDGE,{"disambiguationData":[TD([[subQ2,-1.0]])],"derivedFrom":subQ1}),-1.0]])]});}
            var Q25;
            {var subQ3=sQuery(id+"F6.wireOp",EDGE,"E154.MirrorCS");Q25=makeQuery(id+"F6.imprint","IMPRINT",FACE,{"disambiguationData":[TD([[makeQuery(id+"F6.imprint","IMPRINT",EDGE,{"derivedFrom":subQ3}),1.0]])]});}
            var Q26;
            {var subQ5=sQuery(id+"F6.wireOp",EDGE,"E153.MirrorCS");Q26=makeQuery(id+"F6.imprint","IMPRINT",FACE,{"disambiguationData":[TD([[makeQuery(id+"F6.imprint","IMPRINT",EDGE,{"derivedFrom":subQ5}),-1.0]])]});}
            var Q27;
            {var subQ0=sQuery(id+"F6.wireOp",EDGE,"E135");var subQ1=sQuery(id+"F6.wireOp",EDGE,"E132.top");var subQ2=makeQuery(id+"F6.imprint","INTERSECT",VERTEX,{"derivedFrom":[subQ1,subQ0]});Q27=makeQuery(id+"F6.imprint","IMPRINT",FACE,{"disambiguationData":[TD([[makeQuery(id+"F6.imprint","IMPRINT",EDGE,{"disambiguationData":[TD([[subQ2,-1.0]])],"derivedFrom":subQ1}),-1.0]])]});}
            var Q28;
            {var subQ0=sQuery(id+"F6.wireOp",EDGE,"E159");var subQ1=sQuery(id+"F6.wireOp",EDGE,"E132.top");var subQ2=makeQuery(id+"F6.imprint","INTERSECT",VERTEX,{"derivedFrom":[subQ1,subQ0]});Q28=makeQuery(id+"F6.imprint","IMPRINT",FACE,{"disambiguationData":[TD([[makeQuery(id+"F6.imprint","IMPRINT",EDGE,{"disambiguationData":[TD([[subQ2,-1.0]])],"derivedFrom":subQ1}),-1.0]])]});}
            extrude(context, id + "F7", {"entities" : qUnion([Q0, Q1, Q2, Q3, Q4, Q5, Q6, Q7, Q8, Q9, Q10, Q11, Q12, Q13, Q14, Q15, Q16, Q17, Q18, Q19, Q20, Q21, Q22, Q23, Q24, Q25, Q26, Q27, Q28]), "depth" : 1 * mm});
        }
        {
            var Q0;
            {var subQ1=sQuery(id+"F6.wireOp",EDGE,"E141");Q0=makeQuery(id+"F6.imprint","IMPRINT",FACE,{"disambiguationData":[TD([[makeQuery(id+"F6.imprint","IMPRINT",EDGE,{"derivedFrom":subQ1}),-1.0]])]});}
            var Q1;
            {var subQ0=sQuery(id+"F6.wireOp",EDGE,"E163");var subQ1=sQuery(id+"F6.wireOp",EDGE,"E129");var subQ2=makeQuery(id+"F6.imprint","INTERSECT",VERTEX,{"derivedFrom":[subQ1,subQ0]});Q1=makeQuery(id+"F6.imprint","IMPRINT",FACE,{"disambiguationData":[TD([[makeQuery(id+"F6.imprint","IMPRINT",EDGE,{"disambiguationData":[TD([[subQ2,-1.0]])],"derivedFrom":subQ1}),-1.0]])]});}
            var Q2;
            {var subQ0=sQuery(id+"F6.wireOp",EDGE,"E165");var subQ1=sQuery(id+"F6.wireOp",EDGE,"E129");var subQ2=makeQuery(id+"F6.imprint","INTERSECT",VERTEX,{"derivedFrom":[subQ1,subQ0]});Q2=makeQuery(id+"F6.imprint","IMPRINT",FACE,{"disambiguationData":[TD([[makeQuery(id+"F6.imprint","IMPRINT",EDGE,{"disambiguationData":[TD([[subQ2,-1.0]])],"derivedFrom":subQ1}),-1.0]])]});}
            var Q3;
            {var subQ5=sQuery(id+"F6.wireOp",EDGE,"E144.MirrorCS");Q3=makeQuery(id+"F6.imprint","IMPRINT",FACE,{"disambiguationData":[TD([[makeQuery(id+"F6.imprint","IMPRINT",EDGE,{"derivedFrom":subQ5}),1.0]])]});}
            var Q4;
            Q4=makeQuery(id+"F6.imprint","IMPRINT",FACE,{"disambiguationData":[TD([[makeQuery(id+"F6.imprint","IMPRINT",EDGE,{"derivedFrom":sQuery(id+"F6.wireOp",EDGE,"E144.MirrorCS")}),-1.0]])]});
            var Q5;
            {var subQ0=sQuery(id+"F6.wireOp",EDGE,"E158.MirrorCS");Q5=makeQuery(id+"F6.imprint","IMPRINT",FACE,{"disambiguationData":[TD([[makeQuery(id+"F6.imprint","IMPRINT",EDGE,{"derivedFrom":subQ0}),-1.0]])]});}
            var Q6;
            {var subQ0=sQuery(id+"F6.wireOp",EDGE,"E161");var subQ1=sQuery(id+"F6.wireOp",EDGE,"E130");var subQ2=makeQuery(id+"F6.imprint","INTERSECT",VERTEX,{"derivedFrom":[subQ1,subQ0]});Q6=makeQuery(id+"F6.imprint","IMPRINT",FACE,{"disambiguationData":[TD([[makeQuery(id+"F6.imprint","IMPRINT",EDGE,{"disambiguationData":[TD([[subQ2,-1.0]])],"derivedFrom":subQ1}),-1.0]])]});}
            var Q7;
            {var subQ0=sQuery(id+"F6.wireOp",EDGE,"E135");var subQ1=sQuery(id+"F6.wireOp",EDGE,"E130");var subQ2=makeQuery(id+"F6.imprint","INTERSECT",VERTEX,{"derivedFrom":[subQ1,subQ0]});Q7=makeQuery(id+"F6.imprint","IMPRINT",FACE,{"disambiguationData":[TD([[makeQuery(id+"F6.imprint","IMPRINT",EDGE,{"disambiguationData":[TD([[subQ2,-1.0]])],"derivedFrom":subQ1}),-1.0]])]});}
            var Q8;
            {var subQ0=sQuery(id+"F6.wireOp",EDGE,"E157.MirrorCS");Q8=makeQuery(id+"F6.imprint","IMPRINT",FACE,{"disambiguationData":[TD([[makeQuery(id+"F6.imprint","IMPRINT",EDGE,{"derivedFrom":subQ0}),1.0]])]});}
            var Q9;
            Q9=makeQuery(id+"F6.imprint","IMPRINT",FACE,{"disambiguationData":[TD([[makeQuery(id+"F6.imprint","IMPRINT",EDGE,{"derivedFrom":sQuery(id+"F6.wireOp",EDGE,"E150.MirrorCS")}),1.0]])]});
            var Q10;
            {var subQ5=sQuery(id+"F6.wireOp",EDGE,"E150.MirrorCS");Q10=makeQuery(id+"F6.imprint","IMPRINT",FACE,{"disambiguationData":[TD([[makeQuery(id+"F6.imprint","IMPRINT",EDGE,{"derivedFrom":subQ5}),-1.0]])]});}
            var Q11;
            Q11=makeQuery(id+"F6.imprint","IMPRINT",FACE,{"disambiguationData":[TD([[makeQuery(id+"F6.imprint","IMPRINT",EDGE,{"derivedFrom":sQuery(id+"F6.wireOp",EDGE,"E147.MirrorCS")}),-1.0]])]});
            var Q12;
            {var subQ5=sQuery(id+"F6.wireOp",EDGE,"E147.MirrorCS");Q12=makeQuery(id+"F6.imprint","IMPRINT",FACE,{"disambiguationData":[TD([[makeQuery(id+"F6.imprint","IMPRINT",EDGE,{"derivedFrom":subQ5}),1.0]])]});}
            var Q13;
            {var subQ0=sQuery(id+"F6.wireOp",EDGE,"E135");var subQ1=sQuery(id+"F6.wireOp",EDGE,"E132.top");var subQ2=makeQuery(id+"F6.imprint","INTERSECT",VERTEX,{"derivedFrom":[subQ1,subQ0]});Q13=makeQuery(id+"F6.imprint","IMPRINT",FACE,{"disambiguationData":[TD([[makeQuery(id+"F6.imprint","IMPRINT",EDGE,{"disambiguationData":[TD([[subQ2,-1.0]])],"derivedFrom":subQ1}),1.0]])]});}
            var Q14;
            {var subQ0=sQuery(id+"F6.wireOp",EDGE,"E154.MirrorCS");Q14=makeQuery(id+"F6.imprint","IMPRINT",FACE,{"disambiguationData":[TD([[makeQuery(id+"F6.imprint","IMPRINT",EDGE,{"derivedFrom":subQ0}),-1.0]])]});}
            var Q15;
            {var subQ0=sQuery(id+"F6.wireOp",EDGE,"E153.MirrorCS");Q15=makeQuery(id+"F6.imprint","IMPRINT",FACE,{"disambiguationData":[TD([[makeQuery(id+"F6.imprint","IMPRINT",EDGE,{"derivedFrom":subQ0}),1.0]])]});}
            var Q16;
            {var subQ0=sQuery(id+"F6.wireOp",EDGE,"E159");var subQ1=sQuery(id+"F6.wireOp",EDGE,"E132.top");var subQ2=makeQuery(id+"F6.imprint","INTERSECT",VERTEX,{"derivedFrom":[subQ1,subQ0]});Q16=makeQuery(id+"F6.imprint","IMPRINT",FACE,{"disambiguationData":[TD([[makeQuery(id+"F6.imprint","IMPRINT",EDGE,{"disambiguationData":[TD([[subQ2,-1.0]])],"derivedFrom":subQ1}),1.0]])]});}
            var Q17;
            {var subQ0=sQuery(id+"F6.wireOp",EDGE,"E137");var subQ1=sQuery(id+"F6.wireOp",EDGE,"E135");var subQ2=makeQuery(id+"F6.imprint","INTERSECT",VERTEX,{"derivedFrom":[subQ1,subQ0]});Q17=makeQuery(id+"F6.imprint","IMPRINT",FACE,{"disambiguationData":[TD([[makeQuery(id+"F6.imprint","IMPRINT",EDGE,{"disambiguationData":[TD([[subQ2,-1.0]])],"derivedFrom":subQ1}),-1.0]])]});}
            var Q18;
            {var subQ4=sQuery(id+"F6.wireOp",EDGE,"E163");var subQ5=sQuery(id+"F6.wireOp",EDGE,"E135");var subQ6=makeQuery(id+"F6.imprint","INTERSECT",VERTEX,{"derivedFrom":[subQ5,subQ4]});Q18=makeQuery(id+"F6.imprint","IMPRINT",FACE,{"disambiguationData":[TD([[makeQuery(id+"F6.imprint","IMPRINT",EDGE,{"disambiguationData":[TD([[subQ6,-1.0]])],"derivedFrom":subQ5}),-1.0]])]});}
            var Q19;
            {var subQ0=sQuery(id+"F6.wireOp",EDGE,"E163");var subQ1=sQuery(id+"F6.wireOp",EDGE,"E135");var subQ2=makeQuery(id+"F6.imprint","INTERSECT",VERTEX,{"derivedFrom":[subQ1,subQ0]});Q19=makeQuery(id+"F6.imprint","IMPRINT",FACE,{"disambiguationData":[TD([[makeQuery(id+"F6.imprint","IMPRINT",EDGE,{"disambiguationData":[TD([[subQ2,-1.0]])],"derivedFrom":subQ1}),1.0]])]});}
            var Q20;
            {var subQ0=sQuery(id+"F6.wireOp",EDGE,"E137");var subQ1=sQuery(id+"F6.wireOp",EDGE,"E135");var subQ2=makeQuery(id+"F6.imprint","INTERSECT",VERTEX,{"derivedFrom":[subQ1,subQ0]});Q20=makeQuery(id+"F6.imprint","IMPRINT",FACE,{"disambiguationData":[TD([[makeQuery(id+"F6.imprint","IMPRINT",EDGE,{"disambiguationData":[TD([[subQ2,-1.0]])],"derivedFrom":subQ1}),1.0]])]});}
            extrude(context, id + "F8", {"entities" : qUnion([Q0, Q1, Q2, Q3, Q4, Q5, Q6, Q7, Q8, Q9, Q10, Q11, Q12, Q13, Q14, Q15, Q16, Q17, Q18, Q19, Q20]), "depth" : 1 * mm});
        }
        {
            var Q0;
            Q0=qCreatedBy(makeId("Front.planeOp"),FACE);
            var sketch = newSketch(context, id + "F9", { "sketchPlane" : qUnion([Q0])});
            skCircle(sketch, "E167.cCircle", {"center": v(17.13, 12.43) * mm, "radius": 0.55 * mm, "construction": true});
            skLineSegment(sketch, "E167.0", {"start": v(17.13, 11.87) * mm, "end": v(16.6, 12.25) * mm});
            skLineSegment(sketch, "E167.1", {"start": v(16.6, 12.25) * mm, "end": v(16.8, 12.87) * mm});
            skLineSegment(sketch, "E167.2", {"start": v(16.8, 12.87) * mm, "end": v(17.45, 12.87) * mm});
            skLineSegment(sketch, "E167.3", {"start": v(17.45, 12.87) * mm, "end": v(17.65, 12.25) * mm});
            skLineSegment(sketch, "E167.4", {"start": v(17.65, 12.25) * mm, "end": v(17.13, 11.87) * mm});
            skCircle(sketch, "E168.cCircle", {"center": v(17.13, 12.43) * mm, "radius": 0.76 * mm, "construction": true});
            skLineSegment(sketch, "E168.0", {"start": v(17.13, 11.66) * mm, "end": v(16.4, 12.19) * mm});
            skLineSegment(sketch, "E168.1", {"start": v(16.4, 12.19) * mm, "end": v(16.68, 13.04) * mm});
            skLineSegment(sketch, "E168.2", {"start": v(16.68, 13.04) * mm, "end": v(17.58, 13.04) * mm});
            skLineSegment(sketch, "E168.3", {"start": v(17.58, 13.04) * mm, "end": v(17.86, 12.19) * mm});
            skLineSegment(sketch, "E168.4", {"start": v(17.86, 12.19) * mm, "end": v(17.13, 11.66) * mm});
            skLineSegment(sketch, "E169", {"start": v(15.23, 13.04) * mm, "end": v(16.4, 12.19) * mm});
            skLineSegment(sketch, "E170", {"start": v(16.68, 13.04) * mm, "end": v(15.23, 13.04) * mm});
            skLineSegment(sketch, "E171", {"start": v(15.75, 12.87) * mm, "end": v(16.6, 12.25) * mm});
            skLineSegment(sketch, "E172", {"start": v(15.75, 12.87) * mm, "end": v(16.8, 12.87) * mm});
            skLineSegment(sketch, "E173", {"start": v(16.28, 11.25) * mm, "end": v(16.6, 12.25) * mm});
            skLineSegment(sketch, "E174", {"start": v(16.28, 11.25) * mm, "end": v(17.13, 11.87) * mm});
            skLineSegment(sketch, "E175", {"start": v(15.95, 10.8) * mm, "end": v(17.13, 11.66) * mm});
            skLineSegment(sketch, "E176", {"start": v(15.95, 10.8) * mm, "end": v(16.4, 12.19) * mm});
            skLineSegment(sketch, "E177", {"start": v(17.13, 12.43) * mm, "end": v(17.13, 11.66) * mm});
            skLineSegment(sketch, "E178", {"start": v(17.13, 12.43) * mm, "end": v(16.68, 13.04) * mm});
            skLineSegment(sketch, "E179.MirrorCS", {"start": v(16.68, 13.04) * mm, "end": v(17.13, 14.43) * mm});
            skLineSegment(sketch, "E180.MirrorCS", {"start": v(17.13, 13.87) * mm, "end": v(16.8, 12.87) * mm});
            skLineSegment(sketch, "E181.MirrorCS", {"start": v(17.13, 13.87) * mm, "end": v(17.45, 12.87) * mm});
            skLineSegment(sketch, "E182.MirrorCS", {"start": v(17.13, 14.43) * mm, "end": v(17.58, 13.04) * mm});
            skLineSegment(sketch, "E183.MirrorCS", {"start": v(19.03, 13.04) * mm, "end": v(17.58, 13.04) * mm});
            skLineSegment(sketch, "E184.MirrorCS", {"start": v(18.5, 12.87) * mm, "end": v(17.45, 12.87) * mm});
            skLineSegment(sketch, "E185.MirrorCS", {"start": v(18.5, 12.87) * mm, "end": v(17.65, 12.25) * mm});
            skLineSegment(sketch, "E186.MirrorCS", {"start": v(19.03, 13.04) * mm, "end": v(17.86, 12.19) * mm});
            skLineSegment(sketch, "E187.MirrorCS", {"start": v(17.98, 11.25) * mm, "end": v(17.13, 11.87) * mm});
            skLineSegment(sketch, "E188.MirrorCS", {"start": v(17.98, 11.25) * mm, "end": v(17.65, 12.25) * mm});
            skLineSegment(sketch, "E189.MirrorCS", {"start": v(18.3, 10.8) * mm, "end": v(17.13, 11.66) * mm});
            skLineSegment(sketch, "E190.MirrorCS", {"start": v(18.3, 10.8) * mm, "end": v(17.86, 12.19) * mm});
            skSolve(sketch);
        }
        {
            var Q0;
            {var subQ4=sQuery(id+"F9.wireOp",EDGE,"E167.2");Q0=makeQuery(id+"F9.imprint","IMPRINT",FACE,{"disambiguationData":[TD([[makeQuery(id+"F9.imprint","IMPRINT",EDGE,{"derivedFrom":subQ4}),-1.0]])]});}
            var Q1;
            {var subQ0=sQuery(id+"F9.wireOp",EDGE,"E167.0");Q1=makeQuery(id+"F9.imprint","IMPRINT",FACE,{"disambiguationData":[TD([[makeQuery(id+"F9.imprint","IMPRINT",EDGE,{"derivedFrom":subQ0}),-1.0]])]});}
            var Q2;
            {var subQ0=sQuery(id+"F9.wireOp",EDGE,"E167.1");Q2=makeQuery(id+"F9.imprint","IMPRINT",FACE,{"disambiguationData":[TD([[makeQuery(id+"F9.imprint","IMPRINT",EDGE,{"derivedFrom":subQ0}),1.0]])]});}
            var Q3;
            {var subQ0=sQuery(id+"F9.wireOp",EDGE,"E171");var subQ1=sQuery(id+"F9.wireOp",EDGE,"E168.1");var subQ2=makeQuery(id+"F9.imprint","INTERSECT",VERTEX,{"derivedFrom":[subQ1,subQ0]});Q3=makeQuery(id+"F9.imprint","IMPRINT",FACE,{"disambiguationData":[TD([[makeQuery(id+"F9.imprint","IMPRINT",EDGE,{"disambiguationData":[TD([[subQ2,-1.0]])],"derivedFrom":subQ1}),1.0]])]});}
            var Q4;
            {var subQ0=sQuery(id+"F9.wireOp",EDGE,"E167.0");Q4=makeQuery(id+"F9.imprint","IMPRINT",FACE,{"disambiguationData":[TD([[makeQuery(id+"F9.imprint","IMPRINT",EDGE,{"derivedFrom":subQ0}),1.0]])]});}
            var Q5;
            {var subQ0=sQuery(id+"F9.wireOp",EDGE,"E174");var subQ1=sQuery(id+"F9.wireOp",EDGE,"E168.0");var subQ2=makeQuery(id+"F9.imprint","INTERSECT",VERTEX,{"derivedFrom":[subQ1,subQ0]});Q5=makeQuery(id+"F9.imprint","IMPRINT",FACE,{"disambiguationData":[TD([[makeQuery(id+"F9.imprint","IMPRINT",EDGE,{"disambiguationData":[TD([[subQ2,-1.0]])],"derivedFrom":subQ1}),1.0]])]});}
            var Q6;
            {var subQ0=sQuery(id+"F9.wireOp",EDGE,"E188.MirrorCS");var subQ1=sQuery(id+"F9.wireOp",EDGE,"E168.4");var subQ2=makeQuery(id+"F9.imprint","INTERSECT",VERTEX,{"derivedFrom":[subQ1,subQ0]});Q6=makeQuery(id+"F9.imprint","IMPRINT",FACE,{"disambiguationData":[TD([[makeQuery(id+"F9.imprint","IMPRINT",EDGE,{"disambiguationData":[TD([[subQ2,-1.0]])],"derivedFrom":subQ1}),1.0]])]});}
            var Q7;
            {var subQ0=sQuery(id+"F9.wireOp",EDGE,"E167.4");Q7=makeQuery(id+"F9.imprint","IMPRINT",FACE,{"disambiguationData":[TD([[makeQuery(id+"F9.imprint","IMPRINT",EDGE,{"derivedFrom":subQ0}),1.0]])]});}
            var Q8;
            {var subQ0=sQuery(id+"F9.wireOp",EDGE,"E184.MirrorCS");var subQ1=sQuery(id+"F9.wireOp",EDGE,"E168.3");var subQ2=makeQuery(id+"F9.imprint","INTERSECT",VERTEX,{"derivedFrom":[subQ1,subQ0]});Q8=makeQuery(id+"F9.imprint","IMPRINT",FACE,{"disambiguationData":[TD([[makeQuery(id+"F9.imprint","IMPRINT",EDGE,{"disambiguationData":[TD([[subQ2,-1.0]])],"derivedFrom":subQ1}),1.0]])]});}
            var Q9;
            {var subQ0=sQuery(id+"F9.wireOp",EDGE,"E167.3");Q9=makeQuery(id+"F9.imprint","IMPRINT",FACE,{"disambiguationData":[TD([[makeQuery(id+"F9.imprint","IMPRINT",EDGE,{"derivedFrom":subQ0}),1.0]])]});}
            var Q10;
            {var subQ0=sQuery(id+"F9.wireOp",EDGE,"E167.2");Q10=makeQuery(id+"F9.imprint","IMPRINT",FACE,{"disambiguationData":[TD([[makeQuery(id+"F9.imprint","IMPRINT",EDGE,{"derivedFrom":subQ0}),1.0]])]});}
            var Q11;
            {var subQ0=sQuery(id+"F9.wireOp",EDGE,"E180.MirrorCS");var subQ1=sQuery(id+"F9.wireOp",EDGE,"E168.2");var subQ2=makeQuery(id+"F9.imprint","INTERSECT",VERTEX,{"derivedFrom":[subQ1,subQ0]});Q11=makeQuery(id+"F9.imprint","IMPRINT",FACE,{"disambiguationData":[TD([[makeQuery(id+"F9.imprint","IMPRINT",EDGE,{"disambiguationData":[TD([[subQ2,-1.0]])],"derivedFrom":subQ1}),1.0]])]});}
            extrude(context, id + "F10", {"entities" : qUnion([Q0, Q1, Q2, Q3, Q4, Q5, Q6, Q7, Q8, Q9, Q10, Q11]), "depth" : 1.8 * mm});
        }
        {
            var Q0;
            {var subQ1=sQuery(id+"F9.wireOp",EDGE,"E169");Q0=makeQuery(id+"F9.imprint","IMPRINT",FACE,{"disambiguationData":[TD([[makeQuery(id+"F9.imprint","IMPRINT",EDGE,{"derivedFrom":subQ1}),1.0]])]});}
            var Q1;
            {var subQ1=sQuery(id+"F9.wireOp",EDGE,"E168.2");var subQ3=sQuery(id+"F9.wireOp",EDGE,"E180.MirrorCS");var subQ4=makeQuery(id+"F9.imprint","INTERSECT",VERTEX,{"derivedFrom":[subQ1,subQ3]});Q1=makeQuery(id+"F9.imprint","IMPRINT",FACE,{"disambiguationData":[TD([[makeQuery(id+"F9.imprint","IMPRINT",EDGE,{"disambiguationData":[TD([[subQ4,1.0]])],"derivedFrom":subQ1}),-1.0]])]});}
            var Q2;
            {var subQ1=sQuery(id+"F9.wireOp",EDGE,"E168.2");var subQ3=sQuery(id+"F9.wireOp",EDGE,"E181.MirrorCS");var subQ4=makeQuery(id+"F9.imprint","INTERSECT",VERTEX,{"derivedFrom":[subQ1,subQ3]});Q2=makeQuery(id+"F9.imprint","IMPRINT",FACE,{"disambiguationData":[TD([[makeQuery(id+"F9.imprint","IMPRINT",EDGE,{"disambiguationData":[TD([[subQ4,-1.0]])],"derivedFrom":subQ1}),-1.0]])]});}
            var Q3;
            {var subQ5=sQuery(id+"F9.wireOp",EDGE,"E183.MirrorCS");Q3=makeQuery(id+"F9.imprint","IMPRINT",FACE,{"disambiguationData":[TD([[makeQuery(id+"F9.imprint","IMPRINT",EDGE,{"derivedFrom":subQ5}),1.0]])]});}
            var Q4;
            {var subQ1=sQuery(id+"F9.wireOp",EDGE,"E168.1");var subQ3=sQuery(id+"F9.wireOp",EDGE,"E172");var subQ4=makeQuery(id+"F9.imprint","INTERSECT",VERTEX,{"derivedFrom":[subQ1,subQ3]});Q4=makeQuery(id+"F9.imprint","IMPRINT",FACE,{"disambiguationData":[TD([[makeQuery(id+"F9.imprint","IMPRINT",EDGE,{"disambiguationData":[TD([[subQ4,-1.0]])],"derivedFrom":subQ1}),-1.0]])]});}
            var Q5;
            {var subQ1=sQuery(id+"F9.wireOp",EDGE,"E168.0");var subQ3=sQuery(id+"F9.wireOp",EDGE,"E173");var subQ4=makeQuery(id+"F9.imprint","INTERSECT",VERTEX,{"derivedFrom":[subQ1,subQ3]});Q5=makeQuery(id+"F9.imprint","IMPRINT",FACE,{"disambiguationData":[TD([[makeQuery(id+"F9.imprint","IMPRINT",EDGE,{"disambiguationData":[TD([[subQ4,-1.0]])],"derivedFrom":subQ1}),-1.0]])]});}
            var Q6;
            {var subQ7=sQuery(id+"F9.wireOp",EDGE,"E175");Q6=makeQuery(id+"F9.imprint","IMPRINT",FACE,{"disambiguationData":[TD([[makeQuery(id+"F9.imprint","IMPRINT",EDGE,{"derivedFrom":subQ7}),1.0]])]});}
            var Q7;
            {var subQ5=sQuery(id+"F9.wireOp",EDGE,"E189.MirrorCS");Q7=makeQuery(id+"F9.imprint","IMPRINT",FACE,{"disambiguationData":[TD([[makeQuery(id+"F9.imprint","IMPRINT",EDGE,{"derivedFrom":subQ5}),-1.0]])]});}
            var Q8;
            {var subQ1=sQuery(id+"F9.wireOp",EDGE,"E168.0");var subQ3=sQuery(id+"F9.wireOp",EDGE,"E174");var subQ4=makeQuery(id+"F9.imprint","INTERSECT",VERTEX,{"derivedFrom":[subQ1,subQ3]});Q8=makeQuery(id+"F9.imprint","IMPRINT",FACE,{"disambiguationData":[TD([[makeQuery(id+"F9.imprint","IMPRINT",EDGE,{"disambiguationData":[TD([[subQ4,1.0]])],"derivedFrom":subQ1}),-1.0]])]});}
            var Q9;
            {var subQ1=sQuery(id+"F9.wireOp",EDGE,"E168.4");var subQ3=sQuery(id+"F9.wireOp",EDGE,"E187.MirrorCS");var subQ4=makeQuery(id+"F9.imprint","INTERSECT",VERTEX,{"derivedFrom":[subQ1,subQ3]});Q9=makeQuery(id+"F9.imprint","IMPRINT",FACE,{"disambiguationData":[TD([[makeQuery(id+"F9.imprint","IMPRINT",EDGE,{"disambiguationData":[TD([[subQ4,-1.0]])],"derivedFrom":subQ1}),-1.0]])]});}
            var Q10;
            {var subQ1=sQuery(id+"F9.wireOp",EDGE,"E168.3");var subQ3=sQuery(id+"F9.wireOp",EDGE,"E185.MirrorCS");var subQ4=makeQuery(id+"F9.imprint","INTERSECT",VERTEX,{"derivedFrom":[subQ1,subQ3]});Q10=makeQuery(id+"F9.imprint","IMPRINT",FACE,{"disambiguationData":[TD([[makeQuery(id+"F9.imprint","IMPRINT",EDGE,{"disambiguationData":[TD([[subQ4,-1.0]])],"derivedFrom":subQ1}),-1.0]])]});}
            var Q11;
            {var subQ5=sQuery(id+"F9.wireOp",EDGE,"E179.MirrorCS");Q11=makeQuery(id+"F9.imprint","IMPRINT",FACE,{"disambiguationData":[TD([[makeQuery(id+"F9.imprint","IMPRINT",EDGE,{"derivedFrom":subQ5}),-1.0]])]});}
            extrude(context, id + "F11", {"entities" : qUnion([Q0, Q1, Q2, Q3, Q4, Q5, Q6, Q7, Q8, Q9, Q10, Q11]), "depth" : 1.81 * mm});
        }
    });
